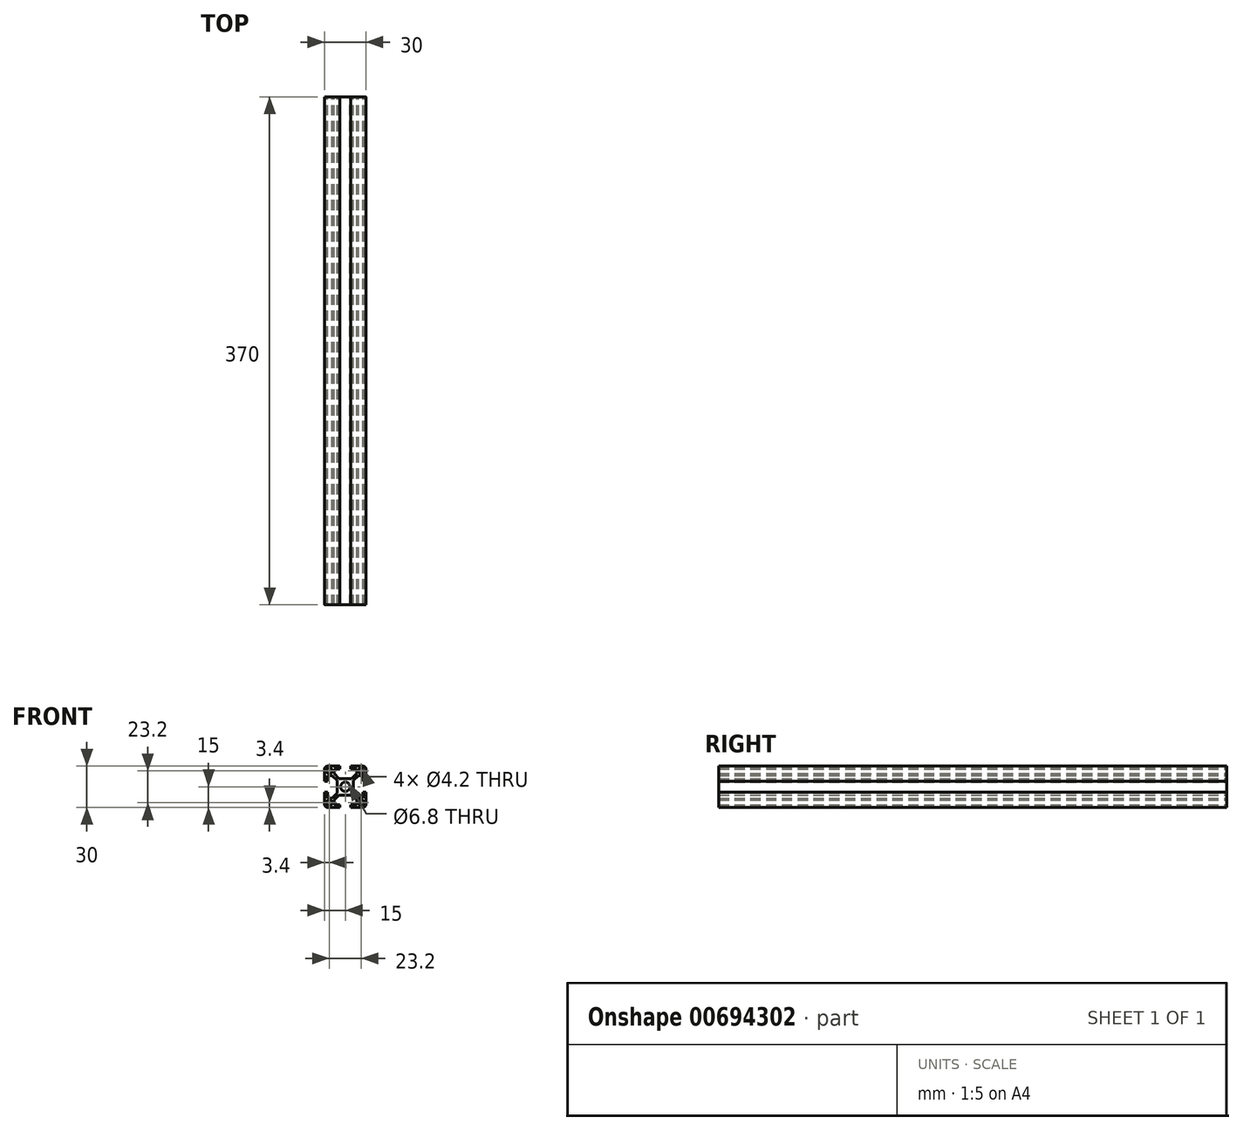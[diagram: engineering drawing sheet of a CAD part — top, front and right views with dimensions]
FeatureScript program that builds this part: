
annotation { "Feature Type Name" : "Feature", "Feature Type Description" : "" }
export const myFeature = defineFeature(function(context is Context, id is Id, definition is map)
    precondition{}
    {
        {
            var Q0;
            Q0=qCreatedBy(makeId("Front.planeOp"),FACE);
            var sketch = newSketch(context, id + "F0", { "sketchPlane" : qUnion([Q0])});
            skLineSegment(sketch, "E0", {"start": v(0, 6) * mm, "end": v(-4.59, 6) * mm});
            skLineSegment(sketch, "E1", {"start": v(-4.59, 6) * mm, "end": v(-8.25, 9.66) * mm});
            skLineSegment(sketch, "E2", {"start": v(-8.25, 9.66) * mm, "end": v(-8.25, 13) * mm});
            skLineSegment(sketch, "E3", {"start": v(-8.25, 13) * mm, "end": v(-4, 13) * mm});
            skLineSegment(sketch, "E4", {"start": v(-4, 13) * mm, "end": v(-4, 15) * mm});
            skLineSegment(sketch, "E5", {"start": v(-4, 15) * mm, "end": v(-13, 15) * mm});
            skLineSegment(sketch, "E6", {"start": v(-15, 13) * mm, "end": v(-15, 4) * mm});
            skLineSegment(sketch, "E7", {"start": v(-15, 4) * mm, "end": v(-13, 4) * mm});
            skLineSegment(sketch, "E8", {"start": v(-13, 4) * mm, "end": v(-13, 8.25) * mm});
            skLineSegment(sketch, "E9", {"start": v(-13, 8.25) * mm, "end": v(-9.66, 8.25) * mm});
            skLineSegment(sketch, "E10", {"start": v(-9.66, 8.25) * mm, "end": v(-6, 4.59) * mm});
            skLineSegment(sketch, "E11", {"start": v(-6, 4.59) * mm, "end": v(-6, 0) * mm});
            skLineSegment(sketch, "E12", {"start": v(-6, 0) * mm, "end": v(0, 0) * mm, "construction": true});
            skLineSegment(sketch, "E13", {"start": v(0, 0) * mm, "end": v(0, 6) * mm, "construction": true});
            skArc(sketch, "E14", {"start": v(0, 3.4) * mm, "mid": v(-2.4, 2.4) * mm, "end": v(-3.4, 0) * mm});
            skCircle(sketch, "E15", {"center": v(-11.6, 11.6) * mm, "radius": 2.1 * mm});
            skLineSegment(sketch, "E16", {"start": v(0, 0) * mm, "end": v(-7.38, 7.38) * mm, "construction": true});
            skLineSegment(sketch, "E17.1.0", {"start": v(-8.25, -13) * mm, "end": v(-8.25, -9.66) * mm});
            skLineSegment(sketch, "E17.1.1", {"start": v(-4, -15) * mm, "end": v(-4, -13) * mm});
            skLineSegment(sketch, "E17.1.2", {"start": v(-4, -13) * mm, "end": v(-8.25, -13) * mm});
            skLineSegment(sketch, "E17.1.3", {"start": v(-15, -4) * mm, "end": v(-15, -13) * mm});
            skLineSegment(sketch, "E17.1.4", {"start": v(-8.25, -9.66) * mm, "end": v(-4.59, -6) * mm});
            skLineSegment(sketch, "E17.1.5", {"start": v(-13, -15) * mm, "end": v(-4, -15) * mm});
            skLineSegment(sketch, "E17.1.6", {"start": v(-4.59, -6) * mm, "end": v(0, -6) * mm});
            skLineSegment(sketch, "E17.1.7", {"start": v(0, -6) * mm, "end": v(0, 0) * mm, "construction": true});
            skLineSegment(sketch, "E17.1.8", {"start": v(0, 0) * mm, "end": v(-6, 0) * mm, "construction": true});
            skLineSegment(sketch, "E17.1.9", {"start": v(-13, -4) * mm, "end": v(-15, -4) * mm});
            skLineSegment(sketch, "E17.1.10", {"start": v(-13, -8.25) * mm, "end": v(-13, -4) * mm});
            skArc(sketch, "E17.1.11", {"start": v(-3.4, 0) * mm, "mid": v(-2.4, -2.4) * mm, "end": v(0, -3.4) * mm});
            skLineSegment(sketch, "E17.1.12", {"start": v(-9.66, -8.25) * mm, "end": v(-13, -8.25) * mm});
            skLineSegment(sketch, "E17.1.13", {"start": v(0, 0) * mm, "end": v(-7.38, -7.38) * mm, "construction": true});
            skLineSegment(sketch, "E17.1.14", {"start": v(-6, -4.59) * mm, "end": v(-9.66, -8.25) * mm});
            skCircle(sketch, "E17.1.15", {"center": v(-11.6, -11.6) * mm, "radius": 2.1 * mm});
            skLineSegment(sketch, "E17.1.16", {"start": v(-6, 0) * mm, "end": v(-6, -4.59) * mm});
            skLineSegment(sketch, "E17.2.0", {"start": v(13, -8.25) * mm, "end": v(9.66, -8.25) * mm});
            skLineSegment(sketch, "E17.2.1", {"start": v(15, -4) * mm, "end": v(13, -4) * mm});
            skLineSegment(sketch, "E17.2.2", {"start": v(13, -4) * mm, "end": v(13, -8.25) * mm});
            skLineSegment(sketch, "E17.2.3", {"start": v(4, -15) * mm, "end": v(13, -15) * mm});
            skLineSegment(sketch, "E17.2.4", {"start": v(9.66, -8.25) * mm, "end": v(6, -4.59) * mm});
            skLineSegment(sketch, "E17.2.5", {"start": v(15, -13) * mm, "end": v(15, -4) * mm});
            skLineSegment(sketch, "E17.2.6", {"start": v(6, -4.59) * mm, "end": v(6, 0) * mm});
            skLineSegment(sketch, "E17.2.7", {"start": v(6, 0) * mm, "end": v(0, 0) * mm, "construction": true});
            skLineSegment(sketch, "E17.2.8", {"start": v(0, 0) * mm, "end": v(0, -6) * mm, "construction": true});
            skLineSegment(sketch, "E17.2.9", {"start": v(4, -13) * mm, "end": v(4, -15) * mm});
            skLineSegment(sketch, "E17.2.10", {"start": v(8.25, -13) * mm, "end": v(4, -13) * mm});
            skArc(sketch, "E17.2.11", {"start": v(0, -3.4) * mm, "mid": v(2.4, -2.4) * mm, "end": v(3.4, 0) * mm});
            skLineSegment(sketch, "E17.2.12", {"start": v(8.25, -9.66) * mm, "end": v(8.25, -13) * mm});
            skLineSegment(sketch, "E17.2.13", {"start": v(0, 0) * mm, "end": v(7.38, -7.38) * mm, "construction": true});
            skLineSegment(sketch, "E17.2.14", {"start": v(4.59, -6) * mm, "end": v(8.25, -9.66) * mm});
            skCircle(sketch, "E17.2.15", {"center": v(11.6, -11.6) * mm, "radius": 2.1 * mm});
            skLineSegment(sketch, "E17.2.16", {"start": v(0, -6) * mm, "end": v(4.59, -6) * mm});
            skLineSegment(sketch, "E17.3.0", {"start": v(8.25, 13) * mm, "end": v(8.25, 9.66) * mm});
            skLineSegment(sketch, "E17.3.1", {"start": v(4, 15) * mm, "end": v(4, 13) * mm});
            skLineSegment(sketch, "E17.3.2", {"start": v(4, 13) * mm, "end": v(8.25, 13) * mm});
            skLineSegment(sketch, "E17.3.3", {"start": v(15, 4) * mm, "end": v(15, 13) * mm});
            skLineSegment(sketch, "E17.3.4", {"start": v(8.25, 9.66) * mm, "end": v(4.59, 6) * mm});
            skLineSegment(sketch, "E17.3.5", {"start": v(13, 15) * mm, "end": v(4, 15) * mm});
            skLineSegment(sketch, "E17.3.6", {"start": v(4.59, 6) * mm, "end": v(0, 6) * mm});
            skLineSegment(sketch, "E17.3.7", {"start": v(0, 6) * mm, "end": v(0, 0) * mm, "construction": true});
            skLineSegment(sketch, "E17.3.8", {"start": v(0, 0) * mm, "end": v(6, 0) * mm, "construction": true});
            skLineSegment(sketch, "E17.3.9", {"start": v(13, 4) * mm, "end": v(15, 4) * mm});
            skLineSegment(sketch, "E17.3.10", {"start": v(13, 8.25) * mm, "end": v(13, 4) * mm});
            skArc(sketch, "E17.3.11", {"start": v(3.4, 0) * mm, "mid": v(2.4, 2.4) * mm, "end": v(0, 3.4) * mm});
            skLineSegment(sketch, "E17.3.12", {"start": v(9.66, 8.25) * mm, "end": v(13, 8.25) * mm});
            skLineSegment(sketch, "E17.3.13", {"start": v(0, 0) * mm, "end": v(7.38, 7.38) * mm, "construction": true});
            skLineSegment(sketch, "E17.3.14", {"start": v(6, 4.59) * mm, "end": v(9.66, 8.25) * mm});
            skCircle(sketch, "E17.3.15", {"center": v(11.6, 11.6) * mm, "radius": 2.1 * mm});
            skLineSegment(sketch, "E17.3.16", {"start": v(6, 0) * mm, "end": v(6, 4.59) * mm});
            skPoint(sketch, "E18.visualSharp", {"position": v(-15, 15) * mm});
            skArc(sketch, "E18.filletArc", {"start": v(-13, 15) * mm, "mid": v(-14.41, 14.41) * mm, "end": v(-15, 13) * mm});
            skPoint(sketch, "E19.visualSharp", {"position": v(15, 15) * mm});
            skArc(sketch, "E19.filletArc", {"start": v(15, 13) * mm, "mid": v(14.41, 14.41) * mm, "end": v(13, 15) * mm});
            skPoint(sketch, "E20.visualSharp", {"position": v(15, -15) * mm});
            skArc(sketch, "E20.filletArc", {"start": v(13, -15) * mm, "mid": v(14.41, -14.41) * mm, "end": v(15, -13) * mm});
            skPoint(sketch, "E21.visualSharp", {"position": v(-15, -15) * mm});
            skArc(sketch, "E21.filletArc", {"start": v(-15, -13) * mm, "mid": v(-14.41, -14.41) * mm, "end": v(-13, -15) * mm});
            skSolve(sketch);
        }
        {
            var Q0;
            Q0=qSketchRegion(id+"F0",true);
            extrude(context, id + "F1", {"entities" : qUnion([Q0]), "depth" : 370 * mm, "offsetDistance" : 25 * mm});
        }
    });
